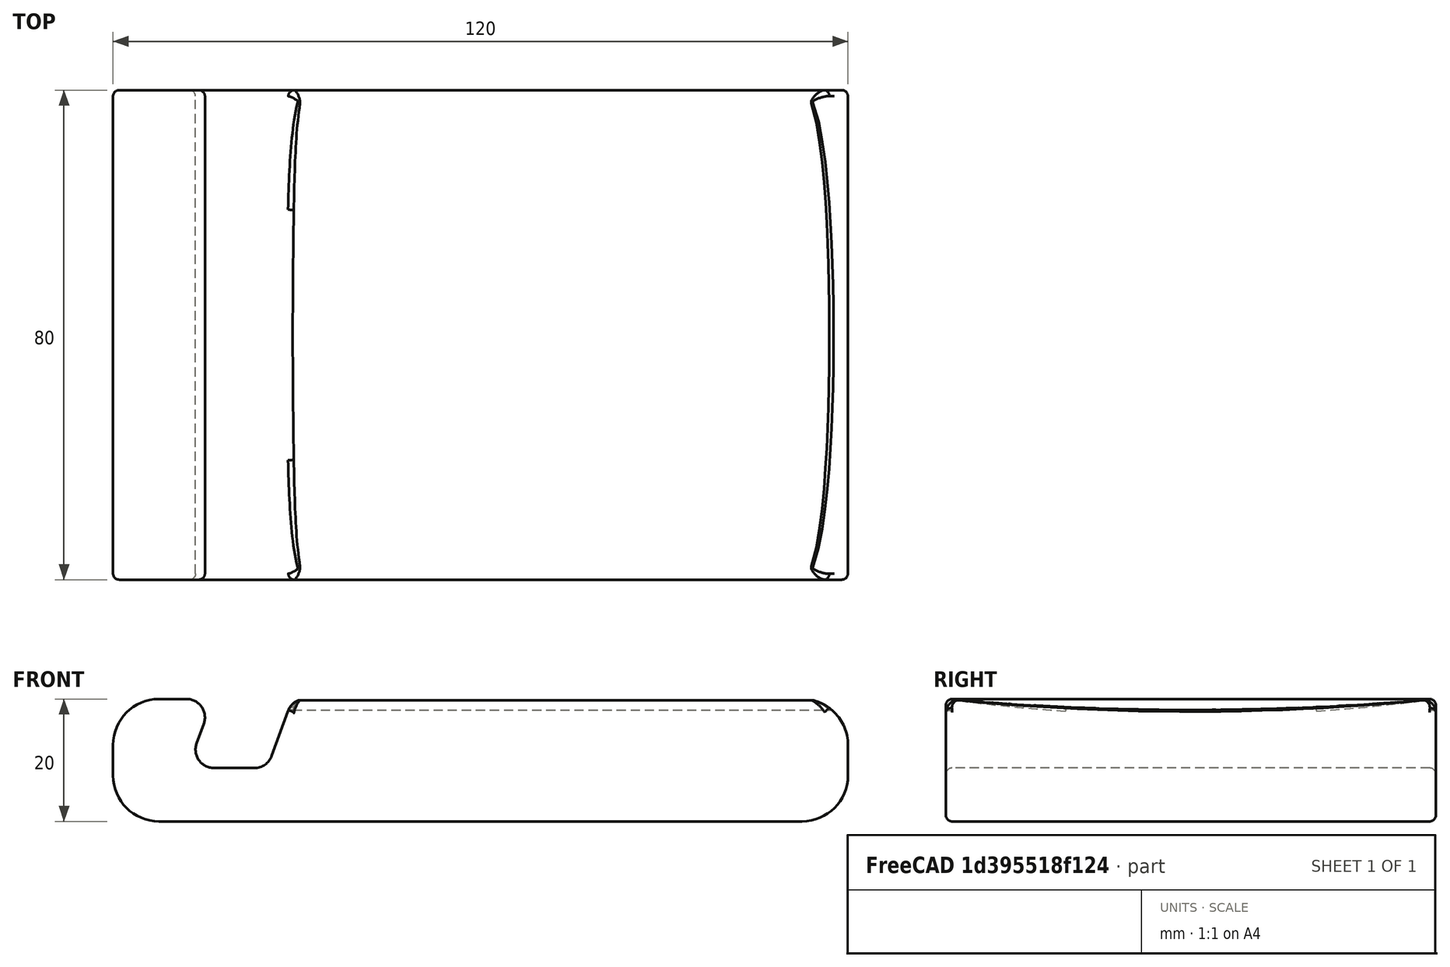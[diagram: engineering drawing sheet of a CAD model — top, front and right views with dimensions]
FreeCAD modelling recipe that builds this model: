
FCSTD DOCUMENT  (FreeCAD 1.0R39319 (Git))
Label: dl_wedge
License: All rights reserved
LicenseURL: https://en.wikipedia.org/wiki/All_rights_reserved
objects: Sketcher::SketchObject×2, PartDesign::Fillet×2, PartDesign::Pad×1, PartDesign::Pocket×1, PartDesign::Body×1, Mesh::Feature×1
note: 17 computed .brp shape members not serialized (recipe doc carries the construction recipe); baked Part::Feature solids carry a one-line shape summary decoded from their .brp

FEATURE [Sketcher::SketchObject] Sketch
  ArcFitTolerance = 1e-06
  AttachmentSupport = -> [XZ_Plane]
  FullyConstrained = true
  MakeInternals = false
  MapMode = 5
  Placement = pos=(0,0,0) rot=(1,0,0;1.5708rad)
  sketch-geometry (23):
    g0: LineSegment StartX=7.5 StartY=0 StartZ=0 EndX=112.5 EndY=0 EndZ=0
    g1: LineSegment StartX=120 StartY=7.5 StartZ=0 EndX=120 EndY=12.5 EndZ=0
    g2: LineSegment StartX=112.5 StartY=20 StartZ=0 EndX=31.3851 EndY=20 EndZ=0
    g3: LineSegment StartX=0 StartY=12.5 StartZ=0 EndX=0 EndY=7.5 EndZ=0
    g4: ArcOfCircle CenterX=7.5 CenterY=12.5 CenterZ=0 NormalX=0 NormalY=0 NormalZ=1 AngleXU=0 Radius=7.5 StartAngle=1.5708 EndAngle=3.14159
    g5: GeomPoint [constr] X=0 Y=20 Z=0
    g6: ArcOfCircle CenterX=7.5 CenterY=7.5 CenterZ=0 NormalX=0 NormalY=0 NormalZ=1 AngleXU=0 Radius=7.5 StartAngle=3.14159 EndAngle=4.71239
    g7: GeomPoint [constr] X=0 Y=0 Z=0
    g8: ArcOfCircle CenterX=112.5 CenterY=7.5 CenterZ=0 NormalX=0 NormalY=0 NormalZ=1 AngleXU=0 Radius=7.5 StartAngle=4.71239 EndAngle=6.28319
    g9: GeomPoint [constr] X=120 Y=0 Z=0
    g10: ArcOfCircle CenterX=112.5 CenterY=12.5 CenterZ=0 NormalX=0 NormalY=0 NormalZ=1 AngleXU=0 Radius=7.5 StartAngle=1e-16 EndAngle=1.5708
    g11: GeomPoint [constr] X=120 Y=20 Z=0
    g12: LineSegment StartX=14.8191 StartY=15.9739 StartZ=0 EndX=13.6456 EndY=12.7497 EndZ=0
    g13: LineSegment StartX=16.4646 StartY=8.72369 StartZ=0 EndX=23.0796 EndY=8.72369 EndZ=0
    g14: LineSegment StartX=25.8987 StartY=10.6976 StartZ=0 EndX=28.566 EndY=18.0261 EndZ=0
    g15: LineSegment StartX=12 StartY=20 StartZ=0 EndX=7.49998 EndY=20 EndZ=0
    g16: ArcOfCircle CenterX=16.4646 CenterY=11.7237 CenterZ=0 NormalX=0 NormalY=0 NormalZ=1 AngleXU=0 Radius=3 StartAngle=2.79253 EndAngle=4.71239
    g17: GeomPoint [constr] X=12.1802 Y=8.72369 Z=0
    g18: ArcOfCircle CenterX=12 CenterY=17 CenterZ=0 NormalX=0 NormalY=0 NormalZ=1 AngleXU=0 Radius=3 StartAngle=5.93412 EndAngle=7.85398
    g19: ArcOfCircle CenterX=31.3851 CenterY=17 CenterZ=0 NormalX=0 NormalY=0 NormalZ=1 AngleXU=0 Radius=3 StartAngle=1.5708 EndAngle=2.79253
    g20: GeomPoint [constr] X=29.2844 Y=20 Z=0
    g21: ArcOfCircle CenterX=23.0796 CenterY=11.7237 CenterZ=0 NormalX=0 NormalY=0 NormalZ=1 AngleXU=0 Radius=3 StartAngle=4.71239 EndAngle=5.93412
    g22: GeomPoint [constr] X=25.1802 Y=8.72369 Z=0
  constraints (54):
    c: Horizontal(g0)
    c: Horizontal(g2)
    c: Vertical(g1)
    c: Vertical(g3)
    c: Distance(g9,g7) = 120  'length'
    c: Distance(g7,g5) = 20  'width'
    c: Coincident(g7,g-1)
    c: PointOnObject(g5,g15)
    c: PointOnObject(g5,g3)
    c: Coincident(g15,g4) = -1.5708
    c: Tangent(g3,g4) = -1.5708
    c: PointOnObject(g7,g0)
    c: PointOnObject(g7,g3)
    c: Tangent(g0,g6) = -1.5708
    c: Tangent(g3,g6) = -1.5708
    c: PointOnObject(g9,g1)
    c: PointOnObject(g9,g0)
    c: Tangent(g1,g8) = -1.5708
    c: Tangent(g0,g8) = -1.5708
    c: PointOnObject(g11,g2)
    c: PointOnObject(g11,g1)
    c: Tangent(g2,g10) = -1.5708
    c: Tangent(g1,g10) = -1.5708
    c: Equal(g10,g8)
    c: Equal(g4,g6)
    c: Equal(g10,g4)
    c: Radius(g10) = 7.5
    c: Horizontal(g13)
    c: Parallel(g12,g14)
    c: Angle(g15,g12) = 1.22173
    c: DistanceX(g17,g22) = 13
    c: Distance(g22,g20) = 12
    c: PointOnObject(g17,g12)
    c: PointOnObject(g17,g13)
    c: Tangent(g12,g16) = -1.5708
    c: Tangent(g13,g16) = -1.5708
    c: Tangent(g12,g18) = 1.5708
    c: Tangent(g15,g18) = -1.5708
    c: PointOnObject(g20,g14)
    c: PointOnObject(g20,g2)
    c: Tangent(g14,g19) = 1.5708
    c: Tangent(g2,g19) = -1.5708
    c: PointOnObject(g22,g14)
    c: PointOnObject(g22,g13)
    c: Tangent(g14,g21) = -1.5708
    c: Tangent(g13,g21) = -1.5708
    c: Parallel(g15,g0)
    c: Distance(g0,g2) = 20
    c: Equal(g18,g16)
    c: Equal(g21,g16)
    c: Equal(g21,g19)
    c: Radius(g19) = 3
    c: Distance(g18,g-2) = 12
    c: DistanceY(g6,g4) = 5
FEATURE [PartDesign::Pad] Pad
  Direction = (0,-1,2e-16)
  Length = 80
  Length2 = 10
  Placement = pos=(0,0,0) rot=(1,0,0;1.5708rad)
  Profile = -> Sketch
  ReferenceAxis = -> Sketch [N_Axis]
  Refine = true
  Suppressed = false
  Type = 0
FEATURE [Sketcher::SketchObject] Sketch001
  ArcFitTolerance = 1e-06
  AttachmentSupport = -> [Pad]
  ExternalGeometry = -> [Pad]
  FullyConstrained = true
  MakeInternals = false
  MapMode = 5
  Placement = pos=(120,0,0) rot=(0.707107,0,0.707107;3.14159rad)
  sketch-geometry (2):
    g0: ArcOfCircle CenterX=468.219 CenterY=40 CenterZ=0 NormalX=0 NormalY=0 NormalZ=1 AngleXU=0 Radius=450 StartAngle=3.05259 EndAngle=3.2306
    g1: LineSegment StartX=20 StartY=80 StartZ=0 EndX=20 EndY=-4.405e-13 EndZ=0
  constraints (5):
    c: Coincident(g0,g-3)
    c: Symmetric(g-6,g-6,g0)
    c: Radius(g0) = 450
    c: Coincident(g1,g0)
    c: Coincident(g1,g0)
FEATURE [PartDesign::Pocket] Pocket
  BaseFeature = -> Pad
  Direction = (-1,0,2e-16)
  Length = 92
  Length2 = 5
  Placement = pos=(0,0,0) rot=(1,0,0;1.5708rad)
  Profile = -> Sketch001
  ReferenceAxis = -> Sketch001 [N_Axis]
  Refine = true
  Suppressed = false
  Type = 0
FEATURE [PartDesign::Fillet] Fillet
  Base = -> Pocket [Edge31,Edge18]
  BaseFeature = -> Pocket
  Placement = pos=(0,0,0) rot=(1,0,0;1.5708rad)
  Radius = 2
  Refine = true
  SupportTransform = false
  Suppressed = false
  UseAllEdges = false
FEATURE [PartDesign::Fillet] Fillet001
  Base = -> Fillet [Edge7]
  BaseFeature = -> Fillet
  Placement = pos=(0,0,0) rot=(1,0,0;1.5708rad)
  Radius = 1
  Refine = true
  SupportTransform = false
  Suppressed = false
  UseAllEdges = false
FEATURE [PartDesign::Body] Body
  AllowCompound = false
  Group = -> [Sketch,Pad,Sketch001,Pocket,Fillet,Fillet001]
  Origin = -> Origin
  Tip = -> Fillet001
FEATURE [Mesh::Feature] dl_wedge_Body  label="dl_wedge-Body"
